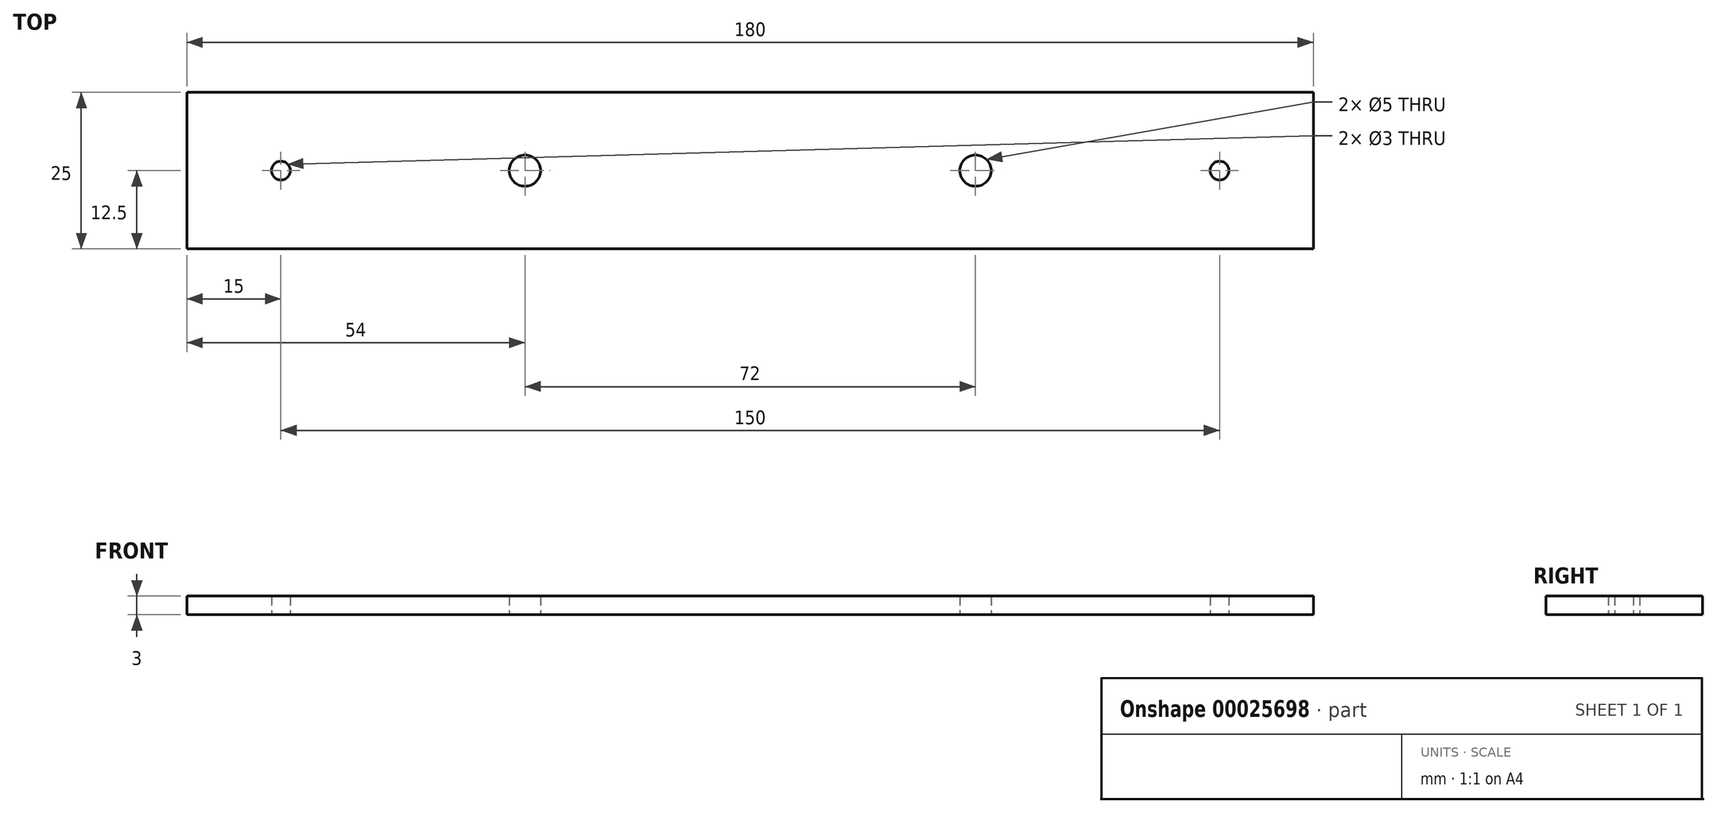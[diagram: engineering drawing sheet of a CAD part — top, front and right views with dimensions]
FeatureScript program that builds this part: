
annotation { "Feature Type Name" : "Feature", "Feature Type Description" : "" }
export const myFeature = defineFeature(function(context is Context, id is Id, definition is map)
    precondition{}
    {
        {
            var Q0;
            Q0=qCreatedBy(makeId("Top.planeOp"),FACE);
            var sketch = newSketch(context, id + "F0", { "sketchPlane" : qUnion([Q0])});
            skLineSegment(sketch, "E0.bottom", {"start": v(90, 12.5) * mm, "end": v(-90, 12.5) * mm});
            skLineSegment(sketch, "E0.top", {"start": v(90, -12.5) * mm, "end": v(-90, -12.5) * mm});
            skLineSegment(sketch, "E0.left", {"start": v(90, 12.5) * mm, "end": v(90, -12.5) * mm});
            skLineSegment(sketch, "E0.right", {"start": v(-90, 12.5) * mm, "end": v(-90, -12.5) * mm});
            skPoint(sketch, "E0.middle", {"position": v(0, 0) * mm});
            skCircle(sketch, "E1", {"center": v(-75, 0) * mm, "radius": 1.5 * mm});
            skCircle(sketch, "E2", {"center": v(-36, 0) * mm, "radius": 2.5 * mm});
            skCircle(sketch, "E3", {"center": v(36, 0) * mm, "radius": 2.5 * mm});
            skCircle(sketch, "E4", {"center": v(75, 0) * mm, "radius": 1.5 * mm});
            skLineSegment(sketch, "E5", {"start": v(-75, 0) * mm, "end": v(-36, 0) * mm, "construction": true});
            skLineSegment(sketch, "E6", {"start": v(0, 0) * mm, "end": v(-36, 0) * mm, "construction": true});
            skLineSegment(sketch, "E7", {"start": v(0, 0) * mm, "end": v(36, 0) * mm, "construction": true});
            skLineSegment(sketch, "E8", {"start": v(75, 0) * mm, "end": v(36, 0) * mm, "construction": true});
            skLineSegment(sketch, "E9", {"start": v(0, 0) * mm, "end": v(0, 12.5) * mm});
            skSolve(sketch);
        }
        {
            var Q0;
            Q0 = qSketchRegion(id + "F0", true);
            extrude(context, id + "F1", {"entities" : qUnion([Q0]), "depth" : 3 * mm});
        }
    });
